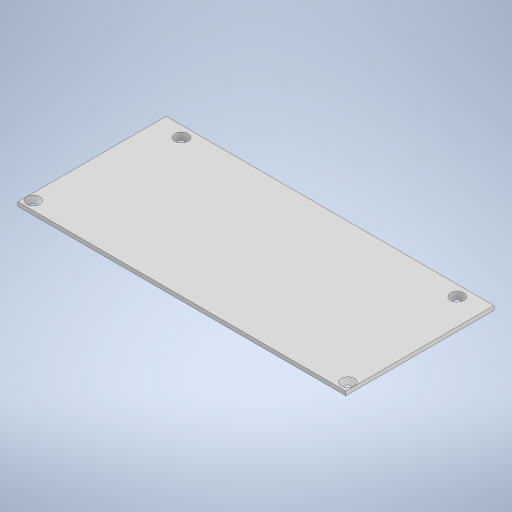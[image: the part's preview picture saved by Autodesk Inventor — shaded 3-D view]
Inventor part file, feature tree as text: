
AUTODESK INVENTOR PART (.ipt)
format: ipt  version: 2024.2 (Build 282272000, 272)  size: 237,568 bytes
history: native  units: in
note: dims shown in document units (in); Inventor stores cm internally (conversion verified against a paired STEP export)
features: extrude x1, chamfer x1, sketch x1
ambient origin geometry x8: Origin, YZ Plane, XZ Plane, XY Plane, X Axis, Y Axis, Z Axis, Center Point
bodies: Solide1 (feature_tree)
feature tree (3):
  extrude  "Extrusion1"  Depth=6.3189in
  chamfer  "Chanfrein1"  Distance=2.8543in
  sketch  "Esquisse1"
